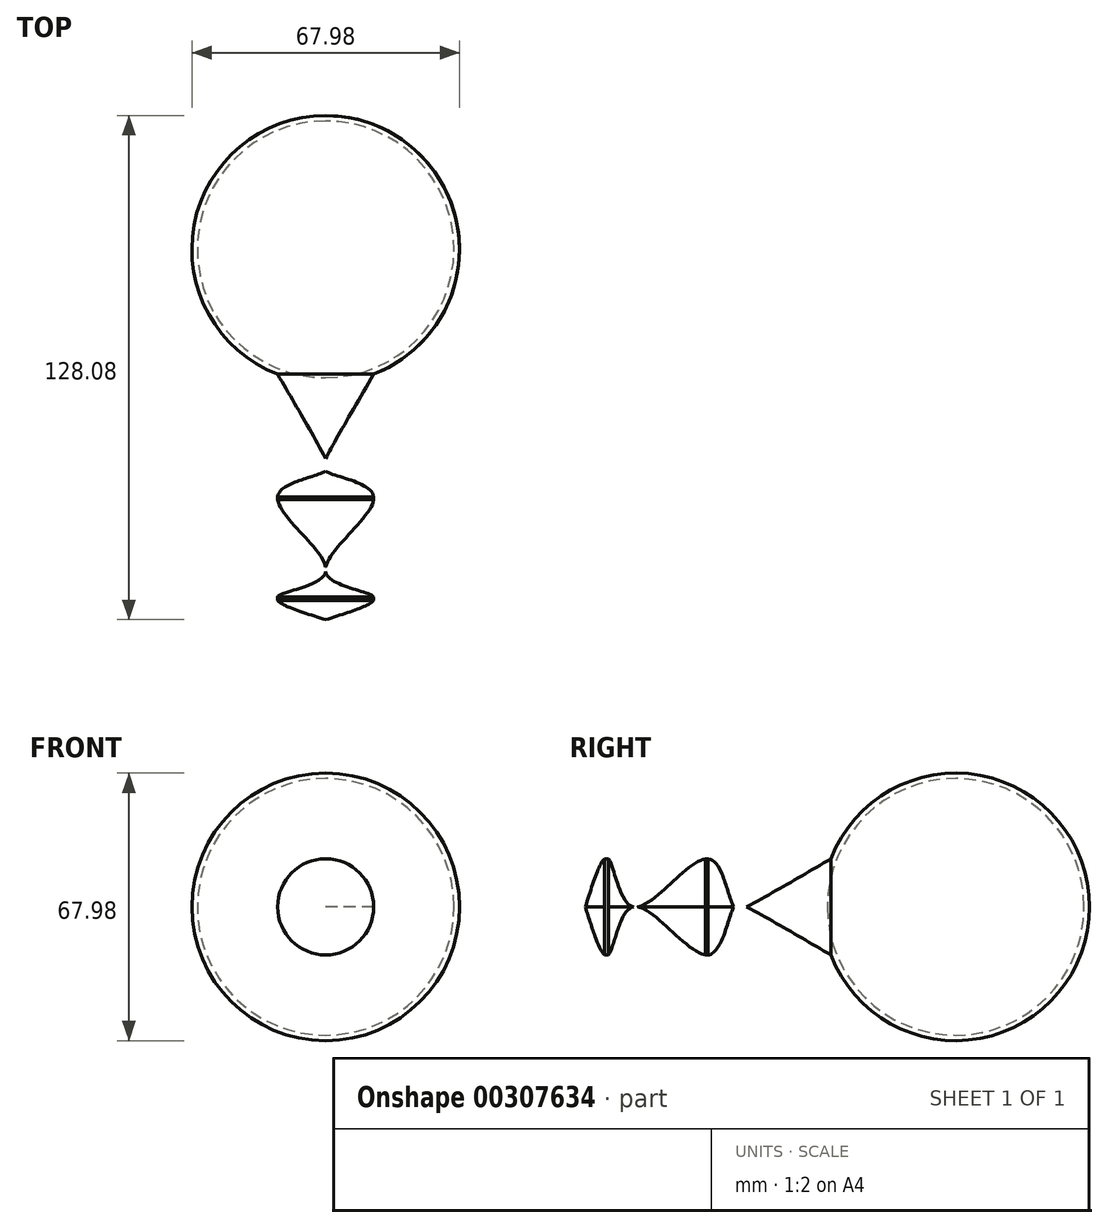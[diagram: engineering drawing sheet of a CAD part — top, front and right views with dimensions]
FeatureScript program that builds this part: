
annotation { "Feature Type Name" : "Feature", "Feature Type Description" : "" }
export const myFeature = defineFeature(function(context is Context, id is Id, definition is map)
    precondition{}
    {
        {
            var Q0;
            Q0=qCreatedBy(makeId("Top.planeOp"),FACE);
            var sketch = newSketch(context, id + "F0", { "sketchPlane" : qUnion([Q0])});
            skArc(sketch, "E0", {"start": v(12.2, 7.04) * mm, "mid": v(33.42, 44.97) * mm, "end": v(0, 72.76) * mm});
            skArc(sketch, "E1", {"start": v(0, 6.16) * mm, "mid": v(32.6, 38.77) * mm, "end": v(0, 71.38) * mm});
            skLineSegment(sketch, "E2", {"start": v(0, 4.78) * mm, "end": v(0, 6.16) * mm});
            skLineSegment(sketch, "E3", {"start": v(0, 72.76) * mm, "end": v(0, 71.38) * mm});
            skLineSegment(sketch, "E4", {"start": v(0, 4.78) * mm, "end": v(0, -55.32) * mm});
            skLineSegment(sketch, "E5", {"start": v(0, 6.16) * mm, "end": v(0, -55.32) * mm});
            skLineSegment(sketch, "E6", {"start": v(12.2, -50.45) * mm, "end": v(12.2, -49.52) * mm});
            skFitSpline(sketch, "E7", {"points": [v(12.2, 7.04) * mm, v(0, -14.38) * mm, v(0, -17.57) * mm, v(12.2, -24.14) * mm, v(0, -43.13) * mm, v(12.2, -49.52) * mm, v(0, -55.32) * mm], "startDerivative": vector(-68.63, -117.98) * mm, "endDerivative": vector(-125.97, -39.07) * mm});
            skLineSegment(sketch, "E8.trimOffspring", {"start": v(12.2, -24.77) * mm, "end": v(12.2, -24.14) * mm});
            skPoint(sketch, "E9.end.orphan", {"position": v(12.2, -55.32) * mm});
            skSolve(sketch);
        }
        {
            var Q0;
            {var subQ4=sQuery(id+"F0.wireOp",EDGE,"E0");Q0=makeQuery(id+"F0.imprint","IMPRINT",FACE,{"disambiguationData":[TD([[makeQuery(id+"F0.imprint","IMPRINT",EDGE,{"derivedFrom":subQ4}),1.0]])]});}
            var Q1;
            {var subQ4=sQuery(id+"F0.wireOp",EDGE,"E8.trimOffspring");Q1=makeQuery(id+"F0.imprint","IMPRINT",FACE,{"disambiguationData":[TD([[makeQuery(id+"F0.imprint","IMPRINT",EDGE,{"derivedFrom":subQ4}),1.0]])]});}
            var Q2;
            {var subQ4=sQuery(id+"F0.wireOp",EDGE,"E6");Q2=makeQuery(id+"F0.imprint","IMPRINT",FACE,{"disambiguationData":[TD([[makeQuery(id+"F0.imprint","IMPRINT",EDGE,{"derivedFrom":subQ4}),1.0]])]});}
            var Q3;
            Q3=sQuery(id+"F0.wireOp",EDGE,"E5");
            revolve(context, id + "F1", {"entities" : qUnion([Q0, Q1, Q2]), "axis" : qUnion([Q3]), "revolveType" : RevolveType.FULL});
        }
    });
